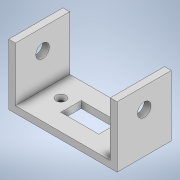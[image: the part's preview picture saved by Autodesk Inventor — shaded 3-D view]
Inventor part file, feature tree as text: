
AUTODESK INVENTOR PART (.ipt)
format: ipt  version: 2022 (Build 260153000, 153)  size: 146,944 bytes
history: native  units: mm
features: extrude x5, sketch x5
ambient origin geometry x8: Origin, YZ Plane, XZ Plane, XY Plane, X Axis, Y Axis, Z Axis, Center Point
bodies: Solid1 (feature_tree)
feature tree (10):
  extrude  "Extrusion1"  Depth=5.0mm
  extrude  "Extrusion2"  Depth=70.0mm
  extrude  "Extrusion3"  Depth=5.0mm
  extrude  "Extrusion4"  Depth=40.0mm TaperAngle=0.0deg
  extrude  "Extrusion5"  Depth=15.0mm
  sketch  "Sketch1"  dims[d0=45.0mm d1=5.0mm]
  sketch  "Sketch2"  dims[d2=40.0mm d3=70.0mm]
  sketch  "Sketch3"  dims[d4=40.0mm d5=5.0mm]
  sketch  "Sketch4"  dims[d6=45.0mm d7=40.0mm d8=0.0mm]
  sketch  "Sketch5"  dims[d9=10.0mm d10=15.0mm d11=20.0mm d12=0.0mm d13=0.0mm d14=28.0mm d15=15.0mm d16=20.0mm d17=35.0mm d18=10.0mm d19=0.0mm d20=7.25mm d21=7.25mm d22=9.0mm d23=9.0mm d24=2.1735mm d25=-7.853982mm d26=2.903mm d27=9.0mm d28=0.0mm d29=0.0mm]
